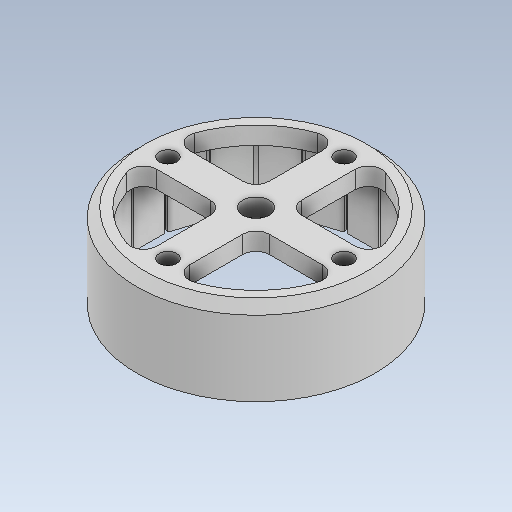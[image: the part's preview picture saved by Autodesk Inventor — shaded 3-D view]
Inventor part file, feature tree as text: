
AUTODESK INVENTOR PART (.ipt)
format: ipt  version: 2020 (Build 240168000, 168)  size: 285,184 bytes
history: native  units: mm
features: sketch x6, other x3
ambient origin geometry x8: Origin, YZ Plane, XZ Plane, XY Plane, X Axis, Y Axis, Z Axis, Center Point
bodies: Solid1 (feature_tree)
feature tree (9):
  other  "mot_27_1.ipt"
  other  "Solid1::mot_27_1.ipt"
  other  "TaggingFeature1"
  sketch  "Sketch1"  dims[d0=10.0mm]
  sketch  "Sketch2"
  sketch  "Sketch3"
  sketch  "Sketch4"
  sketch  "Sketch5"
  sketch  "Sketch6"
